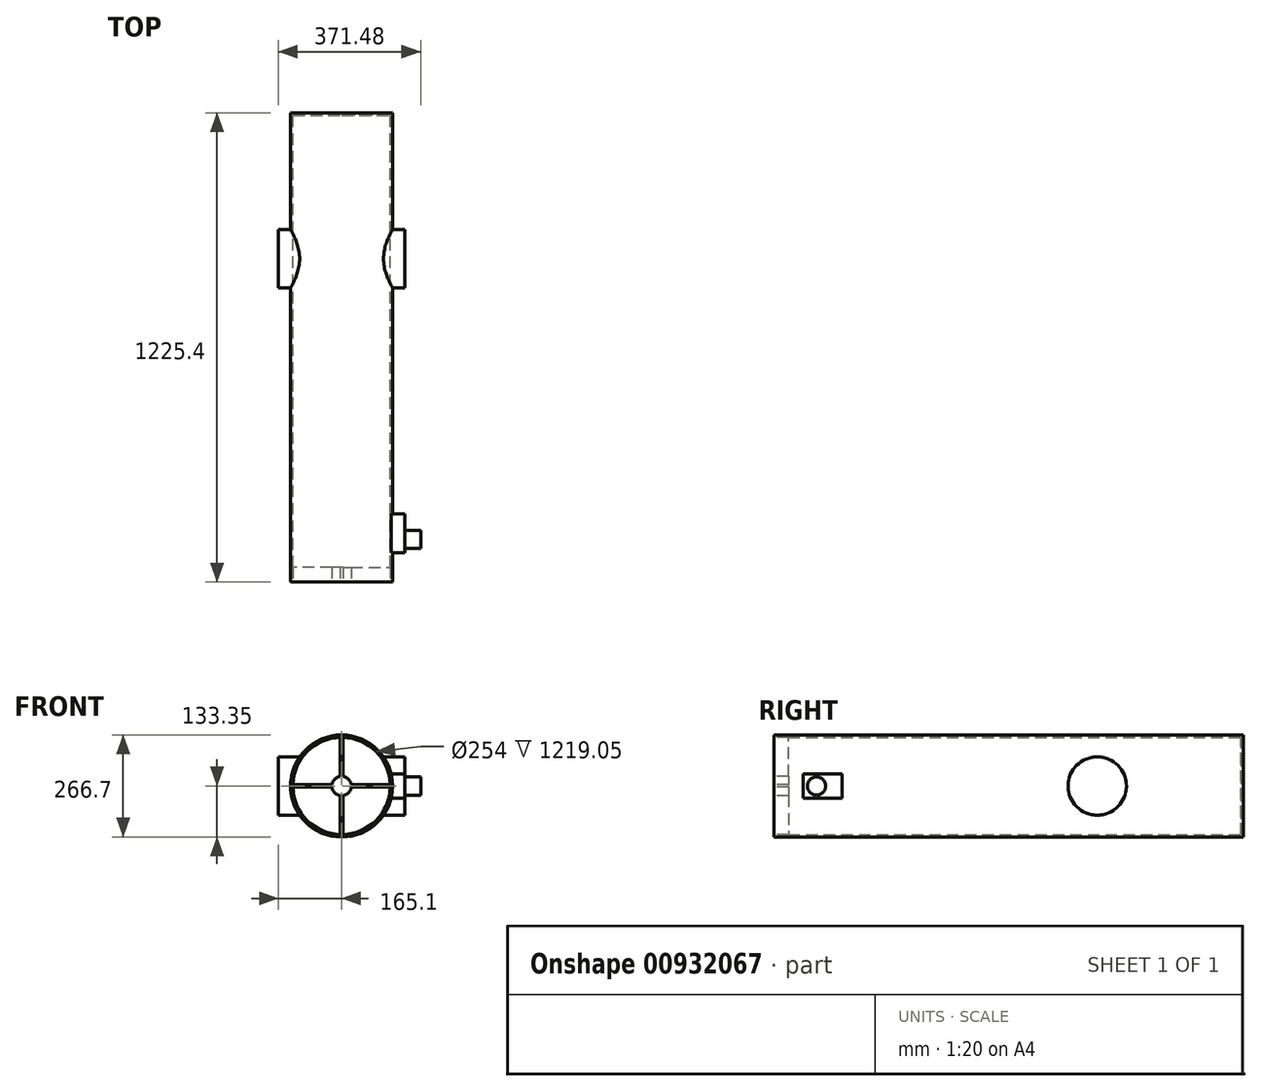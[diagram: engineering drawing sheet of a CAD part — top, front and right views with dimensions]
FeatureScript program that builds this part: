
annotation { "Feature Type Name" : "Feature", "Feature Type Description" : "" }
export const myFeature = defineFeature(function(context is Context, id is Id, definition is map)
    precondition{}
    {
        {
            var Q0;
            Q0=qCreatedBy(makeId("Front.planeOp"),FACE);
            var sketch = newSketch(context, id + "F0", { "sketchPlane" : qUnion([Q0])});
            skCircle(sketch, "E0", {"center": v(0, 0) * mm, "radius": 127 * mm});
            skCircle(sketch, "E1", {"center": v(0, 0) * mm, "radius": 133.35 * mm});
            skSolve(sketch);
        }
        {
            var Q0;
            Q0 = qSketchRegion(id + "F0", true);
            extrude(context, id + "F1", {"entities" : qUnion([Q0]), "depth" : 1200 * mm + 25.4 * mm, "offsetDistance" : 25.4 * mm});
        }
        {
            var Q0;
            Q0=qCreatedBy(makeId("Right.planeOp"),FACE);
            var sketch = newSketch(context, id + "F2", { "sketchPlane" : qUnion([Q0])});
            skCircle(sketch, "E2", {"center": v(-381, 0) * mm, "radius": 76.2 * mm});
            skSolve(sketch);
        }
        {
            var Q0;
            Q0 = qSketchRegion(id + "F2", true);
            extrude(context, id + "F3", {"entities" : qUnion([Q0]), "operationType" : NewBodyOperationType.ADD, "depth" : 165.1 * mm, "offsetDistance" : 25.4 * mm, "hasSecondDirection" : true, "secondDirectionOppositeDirection" : true, "secondDirectionDepth" : 165.1 * mm});
        }
        {
            var Q0;
            Q0=makeQuery(id+"F1.opExtrude","CAP_FACE",FACE,{"disambiguationData":[OSD([sQuery(id+"F0.wireOp",EDGE,"E0"),sQuery(id+"F0.wireOp",EDGE,"E1")])],"isStart":true});
            var sketch = newSketch(context, id + "F4", { "sketchPlane" : qUnion([Q0])});
            skCircle(sketch, "E3.0", {"center": v(0, 0) * mm, "radius": 127 * mm});
            skSolve(sketch);
        }
        {
            var Q0;
            Q0 = qSketchRegion(id + "F4", true);
            extrude(context, id + "F5", {"entities" : qUnion([Q0]), "operationType" : NewBodyOperationType.REMOVE, "endBound" : BoundingType.THROUGH_ALL, "oppositeDirection" : true, "depth" : 25.4 * mm, "offsetDistance" : 25.4 * mm});
        }
        {
            var Q0;
            Q0=makeQuery(id+"F1.opExtrude","CAP_FACE",FACE,{"disambiguationData":[OSD([sQuery(id+"F0.wireOp",EDGE,"E0"),sQuery(id+"F0.wireOp",EDGE,"E1")])],"isStart":true});
            var sketch = newSketch(context, id + "F6", { "sketchPlane" : qUnion([Q0])});
            skCircle(sketch, "E4.0", {"center": v(0, 0) * mm, "radius": 127 * mm});
            skSolve(sketch);
        }
        {
            var Q0;
            Q0 = qSketchRegion(id + "F6", true);
            extrude(context, id + "F7", {"entities" : qUnion([Q0]), "operationType" : NewBodyOperationType.ADD, "oppositeDirection" : true, "depth" : 6.35 * mm, "offsetDistance" : 25.4 * mm});
        }
        {
            var Q0;
            Q0=makeQuery(id+"F1.opExtrude","CAP_FACE",FACE,{"disambiguationData":[OSD([sQuery(id+"F0.wireOp",EDGE,"E0"),sQuery(id+"F0.wireOp",EDGE,"E1")])],"isStart":false});
            var sketch = newSketch(context, id + "F8", { "sketchPlane" : qUnion([Q0])});
            skArc(sketch, "E5", {"start": v(-3.18, 25.2) * mm, "mid": v(-17.96, 17.96) * mm, "end": v(-25.2, 3.17) * mm});
            skLineSegment(sketch, "E6", {"start": v(-3.18, 25.2) * mm, "end": v(-3.18, 126.96) * mm});
            skArc(sketch, "E7.0", {"start": v(3.17, 126.96) * mm, "mid": v(0, 127) * mm, "end": v(-3.18, 126.96) * mm});
            skLineSegment(sketch, "E8", {"start": v(3.17, 25.2) * mm, "end": v(3.17, 126.96) * mm});
            skArc(sketch, "E9.1.0", {"start": v(-126.96, 3.17) * mm, "mid": v(-127, 0) * mm, "end": v(-126.96, -3.18) * mm});
            skLineSegment(sketch, "E9.1.1", {"start": v(-25.2, 3.17) * mm, "end": v(-126.96, 3.17) * mm});
            skLineSegment(sketch, "E9.1.2", {"start": v(-25.2, -3.17) * mm, "end": v(-126.96, -3.17) * mm});
            skArc(sketch, "E9.2.0", {"start": v(-3.17, -126.96) * mm, "mid": v(0, -127) * mm, "end": v(3.18, -126.96) * mm});
            skLineSegment(sketch, "E9.2.1", {"start": v(-3.17, -25.2) * mm, "end": v(-3.17, -126.96) * mm});
            skLineSegment(sketch, "E9.2.2", {"start": v(3.17, -25.2) * mm, "end": v(3.17, -126.96) * mm});
            skArc(sketch, "E9.3.0", {"start": v(126.96, -3.17) * mm, "mid": v(127, 0) * mm, "end": v(126.96, 3.18) * mm});
            skLineSegment(sketch, "E9.3.1", {"start": v(25.2, -3.17) * mm, "end": v(126.96, -3.17) * mm});
            skLineSegment(sketch, "E9.3.2", {"start": v(25.2, 3.17) * mm, "end": v(126.96, 3.17) * mm});
            skArc(sketch, "E10.trimOffspring", {"start": v(-25.2, -3.17) * mm, "mid": v(-17.96, -17.96) * mm, "end": v(-3.17, -25.2) * mm});
            skArc(sketch, "E11.trimOffspring", {"start": v(25.2, 3.17) * mm, "mid": v(17.96, 17.96) * mm, "end": v(3.17, 25.2) * mm});
            skArc(sketch, "E12.trimOffspring", {"start": v(3.18, -25.2) * mm, "mid": v(17.96, -17.96) * mm, "end": v(25.2, -3.17) * mm});
            skSolve(sketch);
        }
        {
            var Q0;
            Q0 = qSketchRegion(id + "F8", true);
            extrude(context, id + "F9", {"entities" : qUnion([Q0]), "operationType" : NewBodyOperationType.ADD, "oppositeDirection" : true, "depth" : 38.1 * mm, "offsetDistance" : 25.4 * mm});
        }
        {
            var Q0;
            Q0=makeQuery(id+"F3.opExtrude","CAP_FACE",FACE,{"disambiguationData":[OSD([sQuery(id+"F2.wireOp",EDGE,"E2")])],"isStart":false});
            var sketch = newSketch(context, id + "F10", { "sketchPlane" : qUnion([Q0])});
            skLineSegment(sketch, "E13.0", {"start": v(-1225.4, -133.35) * mm, "end": v(-1225.4, 133.35) * mm});
            skLineSegment(sketch, "E14.bottom", {"start": v(-1047.6, 31.75) * mm, "end": v(-1149.2, 31.75) * mm});
            skLineSegment(sketch, "E14.top", {"start": v(-1047.6, -31.75) * mm, "end": v(-1149.2, -31.75) * mm});
            skLineSegment(sketch, "E14.left", {"start": v(-1047.6, 31.75) * mm, "end": v(-1047.6, -31.75) * mm});
            skLineSegment(sketch, "E14.right", {"start": v(-1149.2, 31.75) * mm, "end": v(-1149.2, -31.75) * mm});
            skPoint(sketch, "E14.middle", {"position": v(-1098.4, 0) * mm});
            skSolve(sketch);
        }
        {
            var Q0;
            Q0 = qSketchRegion(id + "F10", true);
            var Q1;
            Q1=makeQuery(id+"F1.opExtrude","SWEPT_FACE",FACE,{"disambiguationData":[OSD([sQuery(id+"F0.wireOp",EDGE,"E1")])]});
            extrude(context, id + "F11", {"entities" : qUnion([Q0]), "operationType" : NewBodyOperationType.ADD, "endBound" : BoundingType.UP_TO_SURFACE, "oppositeDirection" : true, "depth" : 25.4 * mm, "endBoundEntityFace" : qUnion([Q1]), "offsetDistance" : 25.4 * mm});
        }
        {
            var Q0;
            Q0=makeQuery(id+"F11.opExtrude","CAP_FACE",FACE,{"disambiguationData":[OSD([sQuery(id+"F10.wireOp",EDGE,"E14.bottom"),sQuery(id+"F10.wireOp",EDGE,"E14.top"),sQuery(id+"F10.wireOp",EDGE,"E14.left"),sQuery(id+"F10.wireOp",EDGE,"E14.right")])],"isStart":true});
            var sketch = newSketch(context, id + "F12", { "sketchPlane" : qUnion([Q0])});
            skCircle(sketch, "E15", {"center": v(-1114.27, 0) * mm, "radius": 23.81 * mm});
            skSolve(sketch);
        }
        {
            var Q0;
            Q0 = qSketchRegion(id + "F12", true);
            extrude(context, id + "F13", {"entities" : qUnion([Q0]), "operationType" : NewBodyOperationType.ADD, "depth" : 41.27 * mm, "offsetDistance" : 25.4 * mm});
        }
    });
